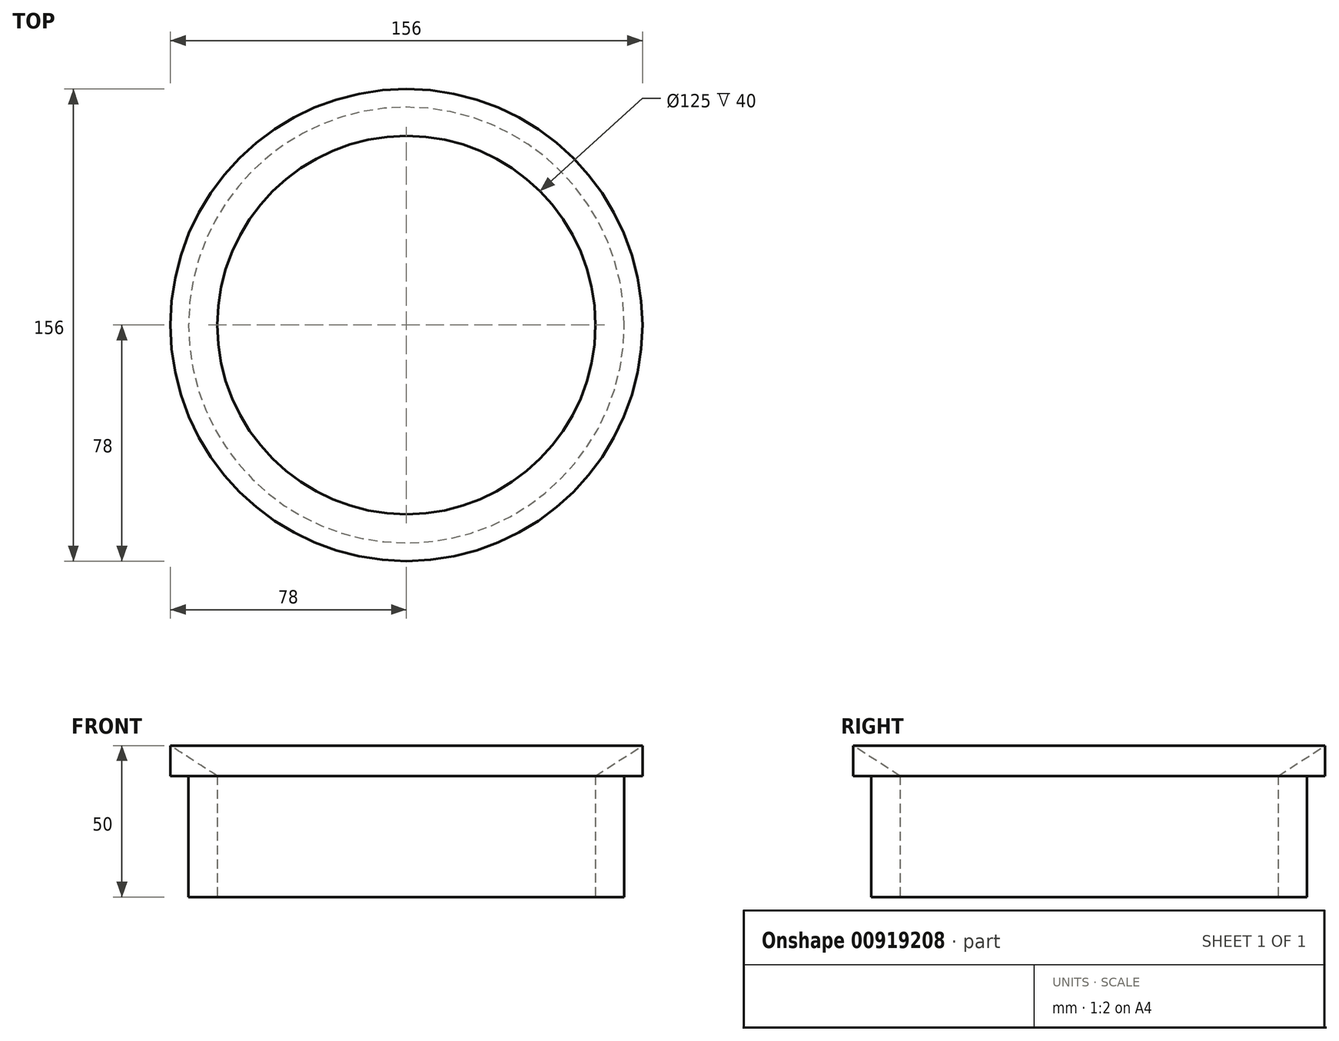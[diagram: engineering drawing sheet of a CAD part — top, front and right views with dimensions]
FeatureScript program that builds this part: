
annotation { "Feature Type Name" : "Feature", "Feature Type Description" : "" }
export const myFeature = defineFeature(function(context is Context, id is Id, definition is map)
    precondition{}
    {
        {
            var Q0;
            Q0=qCreatedBy(makeId("Front.planeOp"),FACE);
            var sketch = newSketch(context, id + "F0", { "sketchPlane" : qUnion([Q0])});
            skLineSegment(sketch, "E0", {"start": v(0, -44.97) * mm, "end": v(-72, -44.97) * mm});
            skLineSegment(sketch, "E1", {"start": v(-72, -44.97) * mm, "end": v(-72, -4.97) * mm});
            skLineSegment(sketch, "E2", {"start": v(-72, -4.97) * mm, "end": v(-78, -4.97) * mm});
            skLineSegment(sketch, "E3", {"start": v(-78, -4.97) * mm, "end": v(-78, 5.03) * mm});
            skLineSegment(sketch, "E4", {"start": v(-78, 5.03) * mm, "end": v(0, 5.03) * mm});
            skLineSegment(sketch, "E5.0", {"start": v(-62.5, -44.97) * mm, "end": v(-62.5, -4.97) * mm});
            skLineSegment(sketch, "E6", {"start": v(-62.5, -4.97) * mm, "end": v(-78, 5.03) * mm});
            skLineSegment(sketch, "E7", {"start": v(0, -44.97) * mm, "end": v(0, 5.03) * mm, "construction": true});
            skSolve(sketch);
        }
        {
            var Q0;
            {var subQ0=sQuery(id+"F0.wireOp",EDGE,"E1");Q0=makeQuery(id+"F0.imprint","IMPRINT",FACE,{"disambiguationData":[TD([[makeQuery(id+"F0.imprint","IMPRINT",EDGE,{"derivedFrom":subQ0}),-1.0]])]});}
            var Q1;
            Q1=sQuery(id+"F0.wireOp",EDGE,"E7");
            revolve(context, id + "F1", {"surfaceOperationType" : NewSurfaceOperationType.NEW, "entities" : qUnion([Q0]), "axis" : qUnion([Q1]), "revolveType" : RevolveType.FULL});
        }
    });
